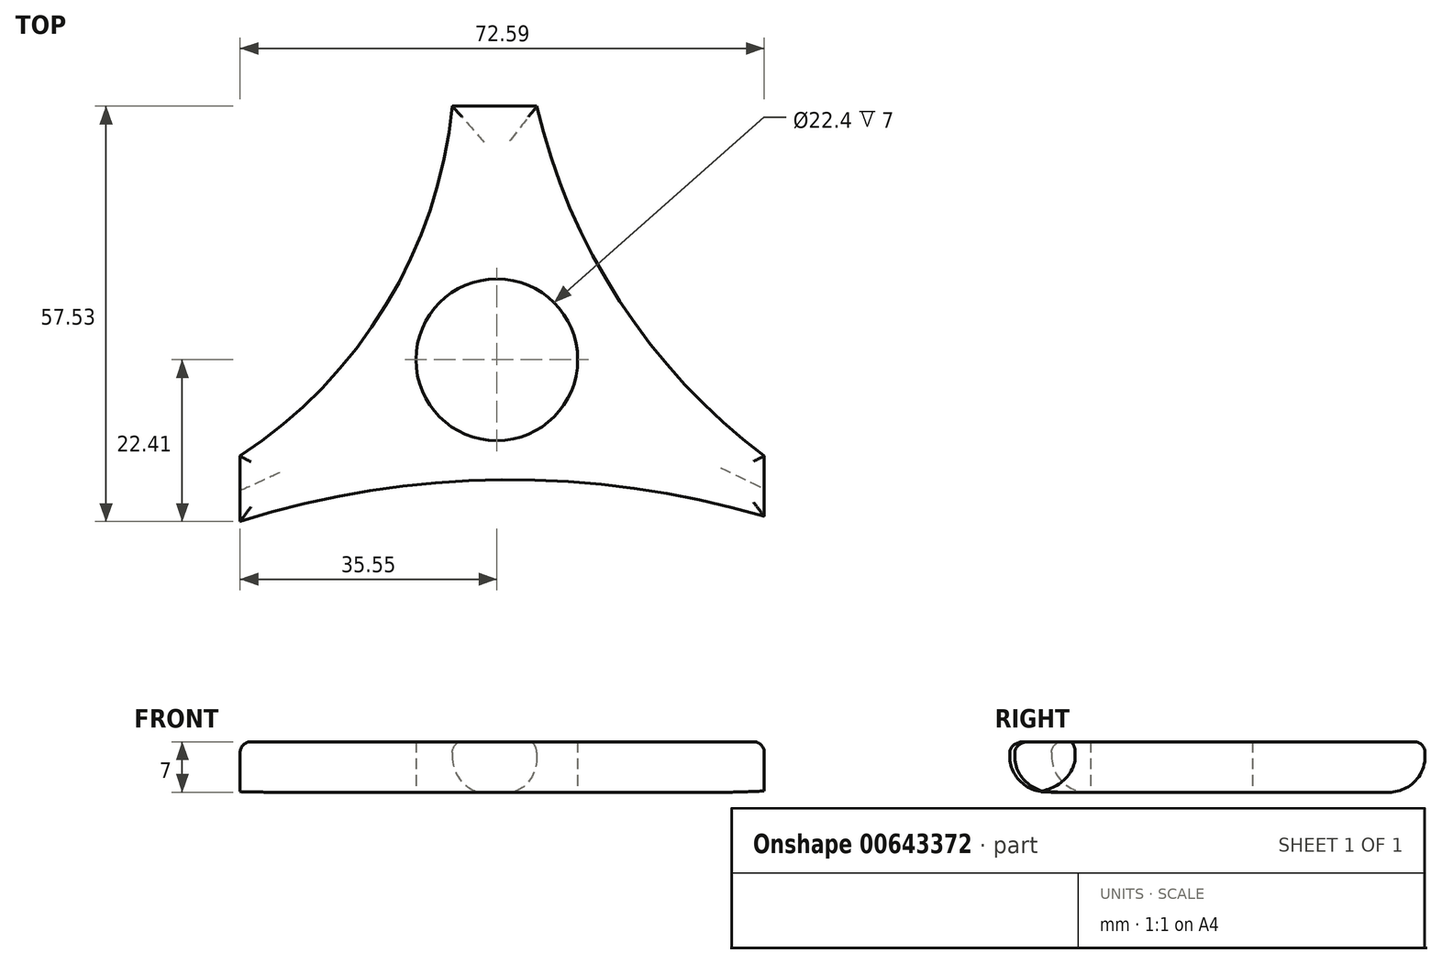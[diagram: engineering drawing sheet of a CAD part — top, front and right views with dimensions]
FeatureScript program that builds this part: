
annotation { "Feature Type Name" : "Feature", "Feature Type Description" : "" }
export const myFeature = defineFeature(function(context is Context, id is Id, definition is map)
    precondition{}
    {
        {
            var Q0;
            Q0=qCreatedBy(makeId("Top.planeOp"),FACE);
            var sketch = newSketch(context, id + "F0", { "sketchPlane" : qUnion([Q0])});
            skCircle(sketch, "E0", {"center": v(0, 0) * mm, "radius": 11.2 * mm});
            skArc(sketch, "E1", {"start": v(-35.55, -13.34) * mm, "mid": v(-15.36, 7.56) * mm, "end": v(-6.16, 35.12) * mm});
            skArc(sketch, "E2", {"start": v(5.55, 35.12) * mm, "mid": v(17.02, 8.1) * mm, "end": v(37.04, -13.34) * mm});
            skArc(sketch, "E3", {"start": v(37.04, -21.71) * mm, "mid": v(0.7, -16.61) * mm, "end": v(-35.55, -22.41) * mm});
            skLineSegment(sketch, "E4", {"start": v(-35.55, -13.34) * mm, "end": v(-35.55, -22.41) * mm});
            skLineSegment(sketch, "E5", {"start": v(37.04, -21.71) * mm, "end": v(37.04, -13.34) * mm});
            skLineSegment(sketch, "E6", {"start": v(-6.16, 35.12) * mm, "end": v(5.55, 35.12) * mm});
            skSolve(sketch);
        }
        {
            var Q0;
            Q0=makeQuery(id+"F0.imprint","IMPRINT",FACE,{"disambiguationData":[TD([[makeQuery(id+"F0.imprint","IMPRINT",EDGE,{"derivedFrom":sQuery(id+"F0.wireOp",EDGE,"E0")}),-1.0]])]});
            extrude(context, id + "F1", {"entities" : qUnion([Q0]), "depth" : 7 * mm, "offsetDistance" : 25 * mm});
        }
        {
            var Q0;
            Q0=makeQuery(id+"F1.opExtrude","CAP_EDGE",EDGE,{"disambiguationData":[OSD([sQuery(id+"F0.wireOp",EDGE,"E4")])],"isStart":false});
            var Q1;
            Q1=makeQuery(id+"F1.opExtrude","CAP_EDGE",EDGE,{"disambiguationData":[OSD([sQuery(id+"F0.wireOp",EDGE,"E3")])],"isStart":false});
            var Q2;
            Q2=makeQuery(id+"F1.opExtrude","CAP_EDGE",EDGE,{"disambiguationData":[OSD([sQuery(id+"F0.wireOp",EDGE,"E1")])],"isStart":false});
            var Q3;
            Q3=makeQuery(id+"F1.opExtrude","CAP_EDGE",EDGE,{"disambiguationData":[OSD([sQuery(id+"F0.wireOp",EDGE,"E2")])],"isStart":false});
            var Q4;
            Q4=makeQuery(id+"F1.opExtrude","CAP_EDGE",EDGE,{"disambiguationData":[OSD([sQuery(id+"F0.wireOp",EDGE,"E5")])],"isStart":false});
            var Q5;
            Q5=makeQuery(id+"F1.opExtrude","CAP_EDGE",EDGE,{"disambiguationData":[OSD([sQuery(id+"F0.wireOp",EDGE,"E6")])],"isStart":false});
            fillet(context, id + "F2", {"entities" : qUnion([Q0, Q1, Q2, Q3, Q4, Q5]), "radius" : 1.5 * mm, "tangentPropagation" : true, "allowEdgeOverflow" : false});
        }
        {
            var Q0;
            Q0=makeQuery(id+"F1.opExtrude","CAP_EDGE",EDGE,{"disambiguationData":[OSD([sQuery(id+"F0.wireOp",EDGE,"E1")])],"isStart":true});
            var Q1;
            Q1=makeQuery(id+"F1.opExtrude","CAP_EDGE",EDGE,{"disambiguationData":[OSD([sQuery(id+"F0.wireOp",EDGE,"E3")])],"isStart":true});
            var Q2;
            Q2=makeQuery(id+"F1.opExtrude","CAP_EDGE",EDGE,{"disambiguationData":[OSD([sQuery(id+"F0.wireOp",EDGE,"E2")])],"isStart":true});
            var Q3;
            Q3=makeQuery(id+"F1.opExtrude","CAP_EDGE",EDGE,{"disambiguationData":[OSD([sQuery(id+"F0.wireOp",EDGE,"E6")])],"isStart":true});
            var Q4;
            Q4=makeQuery(id+"F1.opExtrude","CAP_EDGE",EDGE,{"disambiguationData":[OSD([sQuery(id+"F0.wireOp",EDGE,"E4")])],"isStart":true});
            var Q5;
            Q5=makeQuery(id+"F1.opExtrude","CAP_EDGE",EDGE,{"disambiguationData":[OSD([sQuery(id+"F0.wireOp",EDGE,"E5")])],"isStart":true});
            fillet(context, id + "F3", {"entities" : qUnion([Q0, Q1, Q2, Q3, Q4, Q5]), "radius" : 5 * mm, "tangentPropagation" : true, "allowEdgeOverflow" : false});
        }
    });
